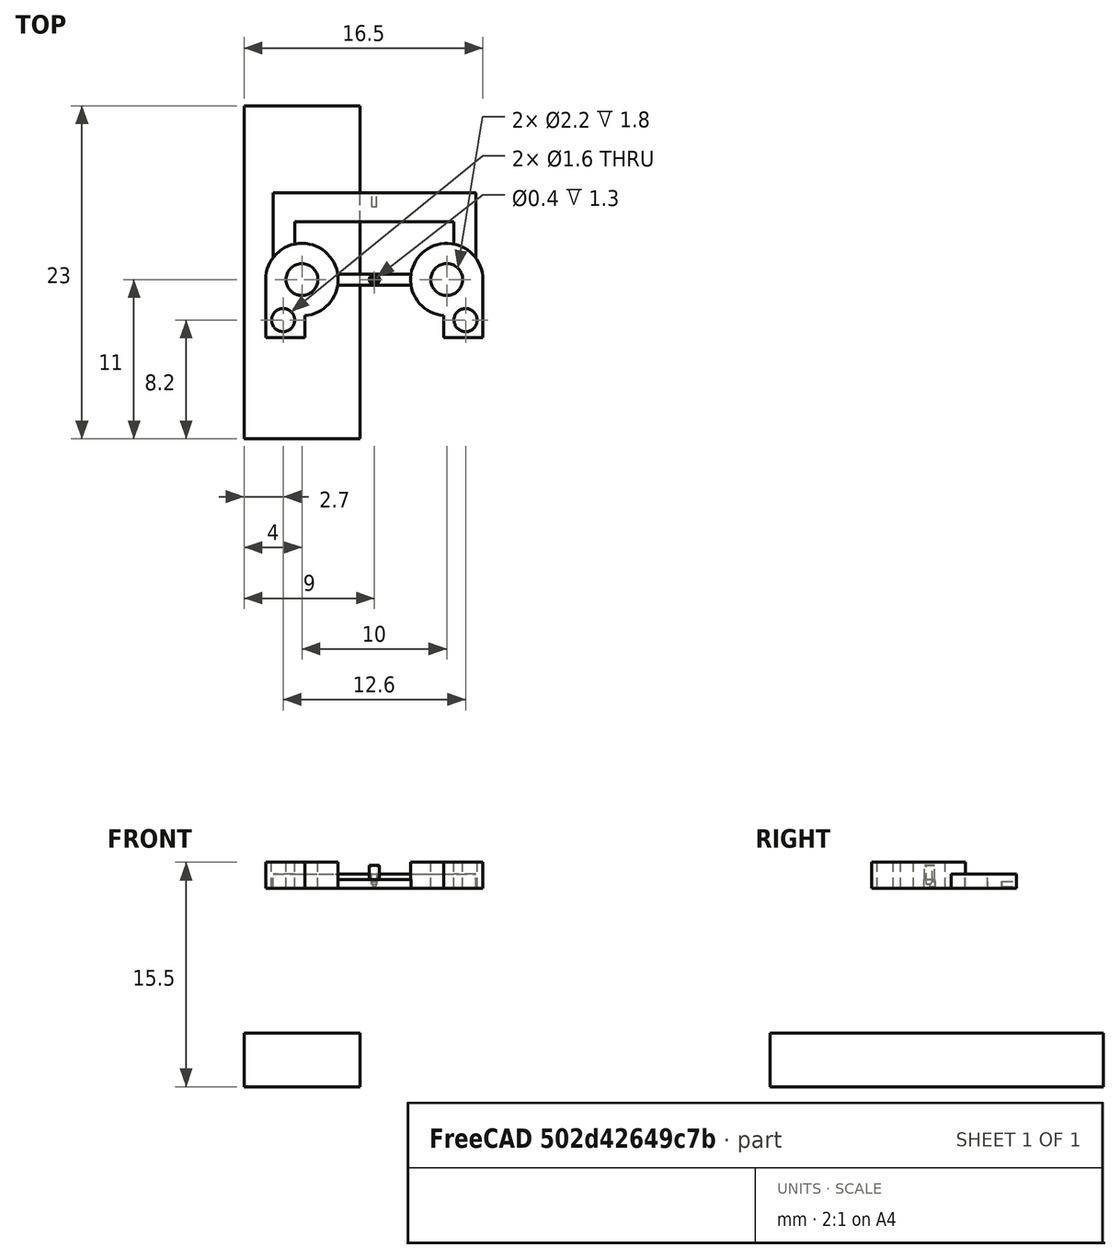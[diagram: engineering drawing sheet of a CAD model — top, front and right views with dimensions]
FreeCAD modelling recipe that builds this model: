
FCSTD DOCUMENT  (FreeCAD 0.18R16033 (Git))
Label: tab
License: All rights reserved
LicenseURL: http://en.wikipedia.org/wiki/All_rights_reserved
objects: Part::Cylinder×5, Path::FeaturePython×4, Part::MultiFuse×3, Part::FeaturePython×2, Part::Box×1, Part::Fillet×1, Part::Cut×1, App::FeaturePython×1, App::DocumentObjectGroup×1, Path::FeatureCompoundPython×1
note: 15 computed .brp shape members not serialized (recipe doc carries the construction recipe); baked Part::Feature solids carry a one-line shape summary decoded from their .brp

FEATURE [Part::Cylinder] Cylinder010  label="ThreadedHole006"
  Angle = 360
  AttacherType = Attacher::AttachEngine3D
  Height = 10
  Placement = pos=(0,8,0) rot=(0,0,1;0rad)
  Radius = 1.55
FEATURE [Part::Cylinder] Cylinder009  label="ThreadedHole005"
  Angle = 360
  AttacherType = Attacher::AttachEngine3D
  Height = 10
  Placement = pos=(0,-7,0) rot=(0,0,1;0rad)
  Radius = 1.55
FEATURE [Part::Box] Box  label="Cube"
  AttacherType = Attacher::AttachEngine3D
  Height = 1.7
  Length = 5
  Placement = pos=(-2.5,-9,0) rot=(0,0,1;0rad)
  Width = 19
FEATURE [Part::MultiFuse] Fusion004
  Placement = pos=(5,0,13) rot=(0,0,1;0rad)
FEATURE [Part::Fillet] Fillet
  Base = -> Box
  Edges = 4 edges r=1: [Edge1,Edge3,Edge5,Edge7]
FEATURE [Part::Cylinder] Cylinder
  Angle = 360
  AttacherType = Attacher::AttachEngine3D
  Height = 10
  Radius = 1
FEATURE [Part::Cylinder] Cylinder011  label="ThreadedHole007"
  Angle = 360
  AttacherType = Attacher::AttachEngine3D
  Height = 1.7
  Placement = pos=(0,8,0) rot=(0,0,1;0rad)
  Radius = 3
FEATURE [Part::Cylinder] Cylinder012  label="ThreadedHole008"
  Angle = 360
  AttacherType = Attacher::AttachEngine3D
  Height = 1.7
  Placement = pos=(0,-7,0) rot=(0,0,1;0rad)
  Radius = 3
FEATURE [Part::MultiFuse] Fusion
  Shapes = -> [Cylinder012,Cylinder011,Fillet]
FEATURE [Part::MultiFuse] Fusion005
  Shapes = -> [Cylinder009,Cylinder010,Cylinder]
FEATURE [Part::Cut] Cut
  Base = -> Fusion
  Tool = -> Fusion005
FEATURE [App::FeaturePython] SetupSheet  # Path/CAM operation (typed FeaturePython)
  ClearanceHeightExpression = OpStockZMax+SetupSheet.ClearanceHeightOffset
  ClearanceHeightOffset = 5
  FinalDepthExpression = OpFinalDepth
  HorizRapid = 0
  SafeHeightExpression = OpStockZMax+SetupSheet.SafeHeightOffset
  SafeHeightOffset = 3
  StartDepthExpression = OpStartDepth
  StepDownExpression = OpToolDiameter
  VertRapid = 0
FEATURE [Part::FeaturePython] Clone  label="Model-Cut"  # Draft clone (typed FeaturePython)
  AttacherType = Attacher::AttachEngine3D
  Fuse = false
  Objects = -> [Cut]
  PathResource = Model
  Scale = (1,1,1)
FEATURE [App::DocumentObjectGroup] Model
  Group = -> [Clone]
FEATURE [Part::FeaturePython] Stock  # WARN: FeaturePython — macro-defined, semantics opaque (R4)
  Base = -> Model
  ExtXneg = 1
  ExtXpos = 1
  ExtYneg = 1
  ExtYpos = 1
  ExtZneg = 1
  ExtZpos = 1
  Placement = pos=(-3,-10,0) rot=(0,0,1;0rad)
  StockType = FromBase
FEATURE [Path::FeaturePython] T3__063_End_Mill  label="T3: 063 End Mill"  # Path/CAM operation (typed FeaturePython)
  HorizFeed = 3
  HorizRapid = 0
  SpindleDir = 0
  SpindleSpeed = 24000
  ToolNumber = 1
  VertFeed = 1
  VertRapid = 0
  expr: HorizRapid = SetupSheet.HorizRapid
  expr: VertRapid = SetupSheet.VertRapid
FEATURE [Path::FeaturePython] Pocket_Shape  # Path/CAM operation (typed FeaturePython)
  Active = true
  AreaParams:
    OpenMode = 0
    Angle = 45.0
    MinArcPoints = 4
    Coplanar = 0
    Tolerance = 1e-07
    CleanDistance = 0.0
    PocketExtraOffset = 0.0
    RoundPrecision = 0.0
    AngleShift = 0.0
    SubjectFill = 0
    PocketMode = 1
    PocketLastStepover = 0.0
    Simplify = False
    SectionTolerance = 1e-06
    MaxArcPoints = 100
    Offset = 0.0
    Accuracy = 0.01
    LastStepover = 0.0
    PocketStepover = 1.58
    ClipFill = 0
    ToolRadius = 0.79
    Outline = False
    ClipperScale = 10000000.0
    FromCenter = True
    Explode = False
    EndType = 0
    Shift = 0.0
    ExtraPass = 0
    Project = False
    JoinType = 0
    Thicken = False
    Stepdown = 1.0
    SectionMode = 2
    MiterLimit = 2.0
    Deflection = 0.01
    Reorient = True
    FitArcs = True
    SectionCount = -1
    SectionOffset = 0.0
    Stepover = 0.0
    Unit = 1.0
    Fill = 0
  Base = -> [Clone]
  ClearanceHeight = 7.7
  CutMode = 0
  ExtraOffset = 0
  FinalDepth = -1
  FinishDepth = 0
  KeepToolDown = false
  MinTravel = false
  OffsetPattern = 0
  OpFinalDepth = 0
  OpStartDepth = 2.7
  OpStockZMax = 2.7
  OpStockZMin = -1
  OpToolDiameter = 1.58
  PathParams = {'resume_height': 5.7, 'feedrate': 3.0, 'verbose': True, 'orientation': 1, 'return_end': True, 'preamble': False, 'retraction': 7.7, 'feedrate_v': 1.0}
  SafeHeight = 5.7
  StartAt = 0
  StartDepth = 2.7
  StartPoint = (0,0,0)
  StepDown = 0.5
  StepOver = 100
  ToolController = -> T3__063_End_Mill
  UseOutline = false
  UseStartPoint = false
  ZigZagAngle = 45
  expr: ClearanceHeight = OpStockZMax + SetupSheet.ClearanceHeightOffset
  expr: SafeHeight = OpStockZMax + SetupSheet.SafeHeightOffset
  expr: StepDown = 0.5
  expr: FinalDepth = -1
  expr: StartDepth = OpStartDepth
FEATURE [Path::FeaturePython] Contour001  # Path/CAM operation (typed FeaturePython)
  Active = true
  AreaParams:
    OpenMode = 0
    Angle = 45.0
    MinArcPoints = 4
    Coplanar = 2
    Tolerance = 1e-07
    CleanDistance = 0.0
    PocketExtraOffset = 0.0
    RoundPrecision = 0.0
    AngleShift = 0.0
    SubjectFill = 0
    PocketMode = 0
    PocketLastStepover = 0.0
    Simplify = False
    SectionTolerance = 1e-06
    MaxArcPoints = 100
    Offset = 0.79
    Accuracy = 0.01
    LastStepover = 0.0
    PocketStepover = 0.0
    ClipFill = 0
    ToolRadius = 1.0
    Outline = False
    ClipperScale = 10000000.0
    FromCenter = False
    Explode = False
    EndType = 0
    Shift = 0.0
    ExtraPass = 0
    Project = False
    JoinType = 0
    Thicken = False
    Stepdown = 1.0
    SectionMode = 2
    MiterLimit = 2.0
    Deflection = 0.01
    Reorient = True
    FitArcs = True
    SectionCount = -1
    SectionOffset = 0.0
    Stepover = 0.0
    Unit = 1.0
    Fill = 0
  ClearanceHeight = 7.7
  Direction = 0
  FinalDepth = -1
  JoinType = 0
  MiterLimit = 0.1
  OffsetExtra = 0
  OpFinalDepth = -1
  OpStartDepth = 2.7
  OpStockZMax = 2.7
  OpStockZMin = -1
  OpToolDiameter = 1.58
  PathParams = {'resume_height': 5.7, 'feedrate': 3.0, 'verbose': True, 'orientation': 1, 'return_end': True, 'preamble': False, 'retraction': 7.7, 'feedrate_v': 1.0}
  SafeHeight = 5.7
  Side = 0
  StartDepth = 2.7
  StartPoint = (0,0,0)
  StepDown = 0.5
  ToolController = -> T3__063_End_Mill
  UseComp = true
  UseStartPoint = false
  expr: ClearanceHeight = OpStockZMax + SetupSheet.ClearanceHeightOffset
  expr: SafeHeight = OpStockZMax + SetupSheet.SafeHeightOffset
  expr: StepDown = 0.5
  expr: FinalDepth = OpFinalDepth
  expr: StartDepth = OpStartDepth
FEATURE [Path::FeatureCompoundPython] Operations  # Path/CAM operation (typed FeaturePython)
  Group = -> [Pocket_Shape,Contour001]
  UsePlacements = false
FEATURE [Path::FeaturePython] Job  # Path/CAM operation (typed FeaturePython)
  GeometryTolerance = 0.01
  Model = -> Model
  Operations = -> Operations
  PostProcessor = 7
  PostProcessorOutputFile = <userpath>/NAS/primary_a/Projects/ion_printer/files/ionprinter/mechanical/bowtie/gcode/tab.ngc
  SetupSheet = -> SetupSheet
  Stock = -> Stock
  ToolController = -> [T3__063_End_Mill]
